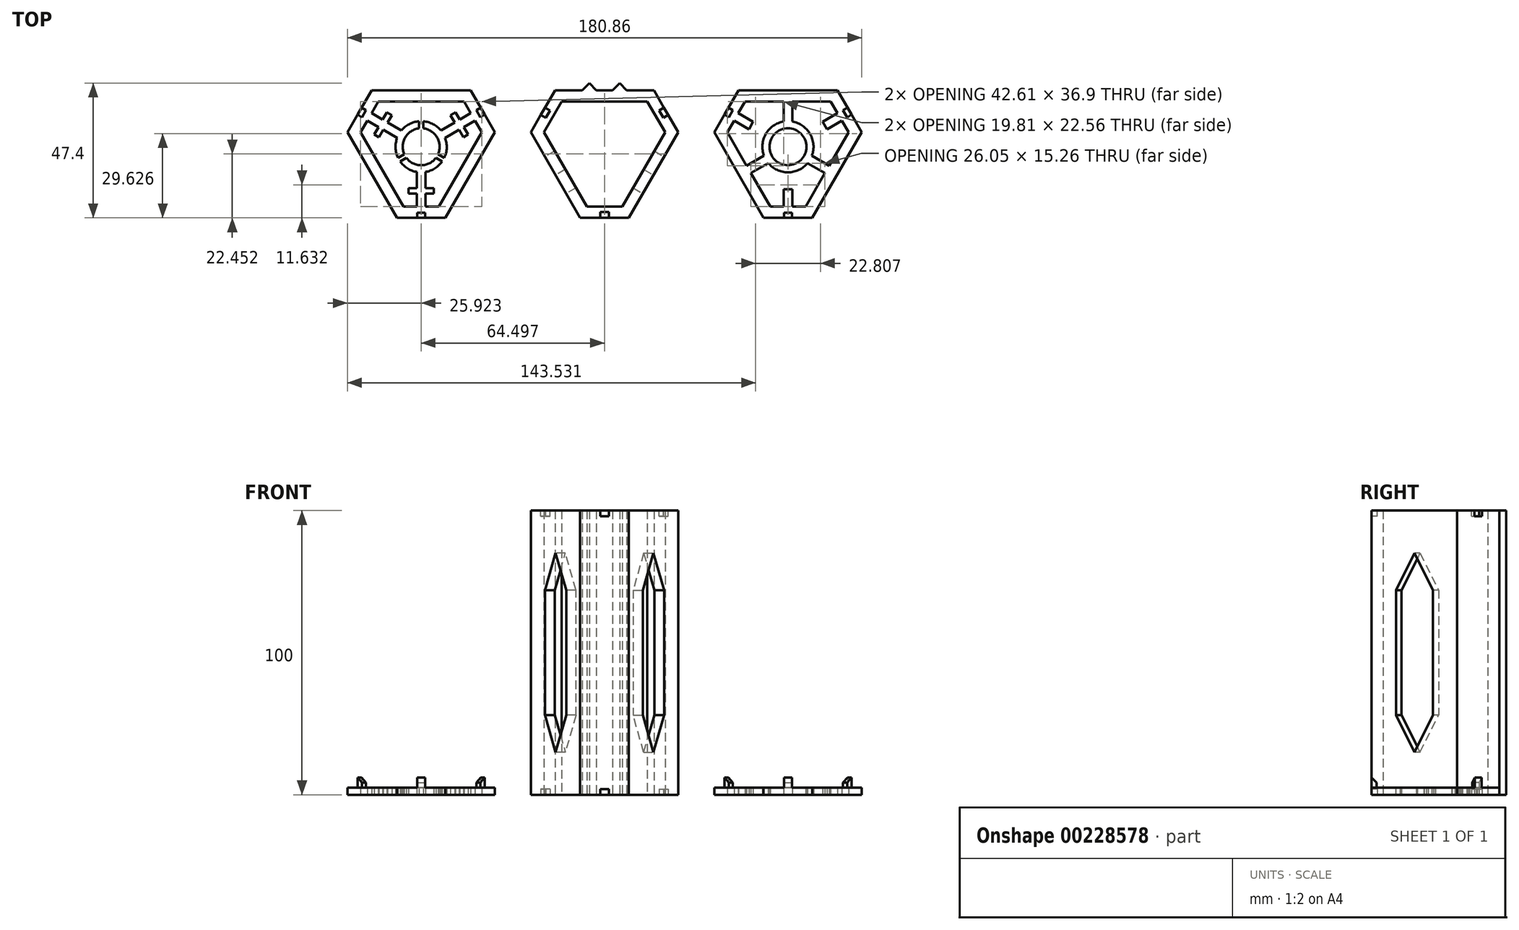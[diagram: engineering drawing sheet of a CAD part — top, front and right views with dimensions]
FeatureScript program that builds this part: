
annotation { "Feature Type Name" : "Feature", "Feature Type Description" : "" }
export const myFeature = defineFeature(function(context is Context, id is Id, definition is map)
    precondition{}
    {
        {
            var Q0;
            Q0=qCreatedBy(makeId("Top.planeOp"),FACE);
            var sketch = newSketch(context, id + "F0", { "sketchPlane" : qUnion([Q0])});
            skCircle(sketch, "E0.cCircle", {"center": v(0, 0) * mm, "radius": 28.87 * mm, "construction": true});
            skLineSegment(sketch, "E0.0", {"start": v(-28.87, 0) * mm, "end": v(-14.43, 25) * mm});
            skLineSegment(sketch, "E0.1", {"start": v(-14.43, 25) * mm, "end": v(14.43, 25) * mm});
            skLineSegment(sketch, "E0.2", {"start": v(14.43, 25) * mm, "end": v(28.87, 0) * mm});
            skLineSegment(sketch, "E0.3", {"start": v(28.87, 0) * mm, "end": v(14.43, -25) * mm});
            skLineSegment(sketch, "E0.4", {"start": v(14.43, -25) * mm, "end": v(-14.43, -25) * mm});
            skLineSegment(sketch, "E0.5", {"start": v(-14.43, -25) * mm, "end": v(-28.87, 0) * mm});
            skCircle(sketch, "E1.cCircle", {"center": v(0, 0) * mm, "radius": 25 * mm, "construction": true});
            skLineSegment(sketch, "E1.0", {"start": v(-21.65, 12.5) * mm, "end": v(21.65, 12.5) * mm});
            skLineSegment(sketch, "E1.1", {"start": v(21.65, 12.5) * mm, "end": v(0, -25) * mm});
            skLineSegment(sketch, "E1.2", {"start": v(0, -25) * mm, "end": v(-21.65, 12.5) * mm});
            skLineSegment(sketch, "E2", {"start": v(-23.62, 9.1) * mm, "end": v(-3.93, -25) * mm});
            skLineSegment(sketch, "E3", {"start": v(-19.69, 15.9) * mm, "end": v(19.69, 15.9) * mm});
            skLineSegment(sketch, "E4", {"start": v(23.62, 9.1) * mm, "end": v(3.93, -25) * mm});
            skLineSegment(sketch, "E5", {"start": v(-25.93, 5.1) * mm, "end": v(-8.55, -25) * mm});
            skLineSegment(sketch, "E6", {"start": v(8.55, -25) * mm, "end": v(25.93, 5.1) * mm});
            skLineSegment(sketch, "E7", {"start": v(-17.38, 19.9) * mm, "end": v(17.38, 19.9) * mm});
            skLineSegment(sketch, "E8", {"start": v(-6.24, -21) * mm, "end": v(6.24, -21) * mm});
            skLineSegment(sketch, "E9", {"start": v(21.3, 5.1) * mm, "end": v(15.07, 15.9) * mm});
            skLineSegment(sketch, "E10", {"start": v(-15.07, 15.9) * mm, "end": v(-21.3, 5.1) * mm});
            skCircle(sketch, "E11.cCircle", {"center": v(-64.5, 0) * mm, "radius": 28.87 * mm, "construction": true});
            skLineSegment(sketch, "E11.0", {"start": v(-93.36, 0) * mm, "end": v(-78.93, 25) * mm});
            skLineSegment(sketch, "E11.1", {"start": v(-78.93, 25) * mm, "end": v(-50.06, 25) * mm});
            skLineSegment(sketch, "E11.2", {"start": v(-50.06, 25) * mm, "end": v(-35.63, 0) * mm});
            skLineSegment(sketch, "E11.3", {"start": v(-35.63, 0) * mm, "end": v(-50.06, -25) * mm});
            skLineSegment(sketch, "E11.4", {"start": v(-50.06, -25) * mm, "end": v(-78.93, -25) * mm});
            skLineSegment(sketch, "E11.5", {"start": v(-78.93, -25) * mm, "end": v(-93.36, 0) * mm});
            skCircle(sketch, "E12.cCircle", {"center": v(-64.5, 0) * mm, "radius": 25 * mm, "construction": true});
            skLineSegment(sketch, "E12.0", {"start": v(-86.15, 12.5) * mm, "end": v(-42.85, 12.5) * mm});
            skLineSegment(sketch, "E12.1", {"start": v(-42.85, 12.5) * mm, "end": v(-64.5, -25) * mm});
            skLineSegment(sketch, "E12.2", {"start": v(-64.5, -25) * mm, "end": v(-86.15, 12.5) * mm});
            skLineSegment(sketch, "E13", {"start": v(-88.11, 9.1) * mm, "end": v(-68.43, -25) * mm});
            skLineSegment(sketch, "E14", {"start": v(-84.18, 15.9) * mm, "end": v(-44.81, 15.9) * mm});
            skLineSegment(sketch, "E15", {"start": v(-40.88, 9.1) * mm, "end": v(-60.57, -25) * mm});
            skLineSegment(sketch, "E16", {"start": v(-90.42, 5.1) * mm, "end": v(-73.05, -25) * mm});
            skLineSegment(sketch, "E17", {"start": v(-55.95, -25) * mm, "end": v(-38.57, 5.1) * mm});
            skLineSegment(sketch, "E18", {"start": v(-81.87, 19.9) * mm, "end": v(-47.12, 19.9) * mm});
            skLineSegment(sketch, "E19", {"start": v(-70.74, -21) * mm, "end": v(-58.26, -21) * mm});
            skLineSegment(sketch, "E20", {"start": v(-43.2, 5.1) * mm, "end": v(-49.43, 15.9) * mm});
            skLineSegment(sketch, "E21", {"start": v(-79.56, 15.9) * mm, "end": v(-85.8, 5.1) * mm});
            skCircle(sketch, "E22.cCircle", {"center": v(64.51, 0) * mm, "radius": 28.87 * mm, "construction": true});
            skLineSegment(sketch, "E22.0", {"start": v(35.65, 0) * mm, "end": v(50.08, 25) * mm});
            skLineSegment(sketch, "E22.1", {"start": v(50.08, 25) * mm, "end": v(78.95, 25) * mm});
            skLineSegment(sketch, "E22.2", {"start": v(78.95, 25) * mm, "end": v(93.38, 0) * mm});
            skLineSegment(sketch, "E22.3", {"start": v(93.38, 0) * mm, "end": v(78.95, -25) * mm});
            skLineSegment(sketch, "E22.4", {"start": v(78.95, -25) * mm, "end": v(50.08, -25) * mm});
            skLineSegment(sketch, "E22.5", {"start": v(50.08, -25) * mm, "end": v(35.65, 0) * mm});
            skCircle(sketch, "E23.cCircle", {"center": v(64.51, 0) * mm, "radius": 25 * mm, "construction": true});
            skLineSegment(sketch, "E23.0", {"start": v(42.86, 12.5) * mm, "end": v(86.17, 12.5) * mm});
            skLineSegment(sketch, "E23.1", {"start": v(86.17, 12.5) * mm, "end": v(64.51, -25) * mm});
            skLineSegment(sketch, "E23.2", {"start": v(64.51, -25) * mm, "end": v(42.86, 12.5) * mm});
            skLineSegment(sketch, "E24", {"start": v(40.9, 9.1) * mm, "end": v(60.58, -25) * mm});
            skLineSegment(sketch, "E25", {"start": v(44.83, 15.9) * mm, "end": v(84.2, 15.9) * mm});
            skLineSegment(sketch, "E26", {"start": v(88.13, 9.1) * mm, "end": v(68.45, -25) * mm});
            skLineSegment(sketch, "E27", {"start": v(38.59, 5.1) * mm, "end": v(55.97, -25) * mm});
            skLineSegment(sketch, "E28", {"start": v(73.06, -25) * mm, "end": v(90.44, 5.1) * mm});
            skLineSegment(sketch, "E29", {"start": v(47.14, 19.9) * mm, "end": v(81.9, 19.9) * mm});
            skLineSegment(sketch, "E30", {"start": v(58.27, -21) * mm, "end": v(70.75, -21) * mm});
            skLineSegment(sketch, "E31", {"start": v(85.82, 5.1) * mm, "end": v(79.58, 15.9) * mm});
            skLineSegment(sketch, "E32", {"start": v(49.45, 15.9) * mm, "end": v(43.2, 5.1) * mm});
            skCircle(sketch, "E33", {"center": v(-64.5, 0) * mm, "radius": 9 * mm});
            skCircle(sketch, "E34", {"center": v(64.51, 0) * mm, "radius": 9 * mm});
            skCircle(sketch, "E35", {"center": v(64.51, 0) * mm, "radius": 6.5 * mm});
            skCircle(sketch, "E36", {"center": v(-64.5, 0) * mm, "radius": 6.5 * mm});
            skPoint(sketch, "E37.startSnap0", {"position": v(53.69, -6.25) * mm});
            skLineSegment(sketch, "E38", {"start": v(51.5, -9.25) * mm, "end": v(57.58, -5.74) * mm});
            skLineSegment(sketch, "E39", {"start": v(50, -6.65) * mm, "end": v(56.08, -3.14) * mm});
            skLineSegment(sketch, "E40", {"start": v(63.01, 15.9) * mm, "end": v(63.01, 8.87) * mm});
            skLineSegment(sketch, "E41", {"start": v(66.01, 15.9) * mm, "end": v(66.01, 8.87) * mm});
            skLineSegment(sketch, "E42", {"start": v(71.45, -5.74) * mm, "end": v(77.54, -9.25) * mm});
            skLineSegment(sketch, "E43", {"start": v(79.04, -6.65) * mm, "end": v(72.95, -3.14) * mm});
            skLineSegment(sketch, "E44", {"start": v(-66, -21) * mm, "end": v(-66, -8.87) * mm});
            skLineSegment(sketch, "E45", {"start": v(-63, -21) * mm, "end": v(-63, -8.87) * mm});
            skLineSegment(sketch, "E46", {"start": v(-47.06, 11.8) * mm, "end": v(-57.56, 5.74) * mm});
            skLineSegment(sketch, "E47", {"start": v(-45.56, 9.2) * mm, "end": v(-56.06, 3.14) * mm});
            skLineSegment(sketch, "E48", {"start": v(-83.43, 9.2) * mm, "end": v(-72.93, 3.14) * mm});
            skLineSegment(sketch, "E49", {"start": v(-81.93, 11.8) * mm, "end": v(-71.43, 5.74) * mm});
            skLineSegment(sketch, "E50", {"start": v(-74.95, -6.9) * mm, "end": v(-69.71, -3.88) * mm});
            skLineSegment(sketch, "E51", {"start": v(-75.7, -5.6) * mm, "end": v(-70.46, -2.58) * mm});
            skLineSegment(sketch, "E52", {"start": v(-54.05, -6.9) * mm, "end": v(-59.28, -3.88) * mm});
            skLineSegment(sketch, "E53", {"start": v(-53.3, -5.6) * mm, "end": v(-58.53, -2.58) * mm});
            skLineSegment(sketch, "E54", {"start": v(-65.25, 12.5) * mm, "end": v(-65.25, 6.46) * mm});
            skLineSegment(sketch, "E55", {"start": v(-63.75, 12.5) * mm, "end": v(-63.75, 6.46) * mm});
            skLineSegment(sketch, "E56", {"start": v(86.17, 12.5) * mm, "end": v(72.3, 4.5) * mm});
            skLineSegment(sketch, "E57", {"start": v(42.86, 12.5) * mm, "end": v(56.72, 4.5) * mm});
            skLineSegment(sketch, "E58", {"start": v(64.51, -25) * mm, "end": v(64.51, -9) * mm});
            skLineSegment(sketch, "E59", {"start": v(51.52, 7.5) * mm, "end": v(52.27, 8.8) * mm});
            skLineSegment(sketch, "E60", {"start": v(51.52, 7.5) * mm, "end": v(50.77, 6.2) * mm});
            skLineSegment(sketch, "E61", {"start": v(77.5, 7.5) * mm, "end": v(76.76, 8.8) * mm});
            skLineSegment(sketch, "E62", {"start": v(77.5, 7.5) * mm, "end": v(78.26, 6.2) * mm});
            skLineSegment(sketch, "E63", {"start": v(64.51, -15) * mm, "end": v(63.01, -15) * mm});
            skLineSegment(sketch, "E64", {"start": v(64.51, -15) * mm, "end": v(66.01, -15) * mm});
            skLineSegment(sketch, "E65", {"start": v(50.77, 6.2) * mm, "end": v(45.58, 9.2) * mm});
            skLineSegment(sketch, "E66", {"start": v(52.27, 8.8) * mm, "end": v(47.08, 11.8) * mm});
            skLineSegment(sketch, "E67", {"start": v(76.76, 8.8) * mm, "end": v(81.95, 11.8) * mm});
            skLineSegment(sketch, "E68", {"start": v(78.26, 6.2) * mm, "end": v(83.45, 9.2) * mm});
            skLineSegment(sketch, "E69", {"start": v(66.01, -15) * mm, "end": v(66.01, -21) * mm});
            skLineSegment(sketch, "E70", {"start": v(63.01, -15) * mm, "end": v(63.01, -21) * mm});
            skLineSegment(sketch, "E71", {"start": v(-78.04, 9.55) * mm, "end": v(-76.54, 12.15) * mm});
            skLineSegment(sketch, "E72", {"start": v(-79.54, 6.95) * mm, "end": v(-81.04, 4.35) * mm});
            skLineSegment(sketch, "E73", {"start": v(-66, -16.5) * mm, "end": v(-69, -16.5) * mm});
            skLineSegment(sketch, "E74", {"start": v(-63, -16.5) * mm, "end": v(-60, -16.5) * mm});
            skLineSegment(sketch, "E75", {"start": v(-51.19, 5.95) * mm, "end": v(-49.69, 3.35) * mm});
            skLineSegment(sketch, "E76", {"start": v(-52.69, 8.55) * mm, "end": v(-54.19, 11.15) * mm});
            skLineSegment(sketch, "E77", {"start": v(-81.04, 4.35) * mm, "end": v(-79.3, 3.35) * mm});
            skLineSegment(sketch, "E78", {"start": v(-79.3, 3.35) * mm, "end": v(-77.8, 5.95) * mm});
            skLineSegment(sketch, "E79", {"start": v(-76.54, 12.15) * mm, "end": v(-74.8, 11.15) * mm});
            skLineSegment(sketch, "E80", {"start": v(-74.8, 11.15) * mm, "end": v(-76.3, 8.55) * mm});
            skLineSegment(sketch, "E81", {"start": v(-54.19, 11.15) * mm, "end": v(-52.46, 12.15) * mm});
            skLineSegment(sketch, "E82", {"start": v(-52.46, 12.15) * mm, "end": v(-50.96, 9.55) * mm});
            skLineSegment(sketch, "E83", {"start": v(-49.69, 3.35) * mm, "end": v(-47.96, 4.35) * mm});
            skLineSegment(sketch, "E84", {"start": v(-47.96, 4.35) * mm, "end": v(-49.46, 6.95) * mm});
            skLineSegment(sketch, "E85", {"start": v(-69, -16.5) * mm, "end": v(-69, -14.5) * mm});
            skLineSegment(sketch, "E86", {"start": v(-69, -14.5) * mm, "end": v(-66, -14.5) * mm});
            skLineSegment(sketch, "E87", {"start": v(-60, -16.5) * mm, "end": v(-60, -14.5) * mm});
            skLineSegment(sketch, "E88", {"start": v(-60, -14.5) * mm, "end": v(-63, -14.5) * mm});
            skLineSegment(sketch, "E89", {"start": v(-78.04, 9.55) * mm, "end": v(-79.54, 6.95) * mm});
            skLineSegment(sketch, "E90", {"start": v(-50.96, 9.55) * mm, "end": v(-49.46, 6.95) * mm});
            skLineSegment(sketch, "E91", {"start": v(-63, -16.5) * mm, "end": v(-66, -16.5) * mm});
            skLineSegment(sketch, "E92", {"start": v(-78.79, 8.25) * mm, "end": v(-82.68, 10.5) * mm});
            skLineSegment(sketch, "E93", {"start": v(-46.31, 10.5) * mm, "end": v(-50.2, 8.25) * mm});
            skLineSegment(sketch, "E94", {"start": v(-64.5, -16.5) * mm, "end": v(-64.5, -21) * mm});
            skLineSegment(sketch, "E95", {"start": v(0, 19.9) * mm, "end": v(-2.84, 19.9) * mm});
            skLineSegment(sketch, "E96", {"start": v(0, 19.9) * mm, "end": v(2.84, 19.9) * mm});
            skLineSegment(sketch, "E97", {"start": v(2.84, 19.9) * mm, "end": v(5.34, 22.4) * mm});
            skLineSegment(sketch, "E98", {"start": v(5.34, 22.4) * mm, "end": v(7.84, 19.9) * mm});
            skLineSegment(sketch, "E99", {"start": v(-2.84, 19.9) * mm, "end": v(-5.34, 22.4) * mm});
            skLineSegment(sketch, "E100", {"start": v(-5.34, 22.4) * mm, "end": v(-7.84, 19.9) * mm});
            skLineSegment(sketch, "E101", {"start": v(-86.15, 12.5) * mm, "end": v(-84.59, 11.6) * mm});
            skLineSegment(sketch, "E102", {"start": v(-84.59, 11.6) * mm, "end": v(-83.89, 12.81) * mm});
            skLineSegment(sketch, "E103", {"start": v(-83.89, 12.81) * mm, "end": v(-85.45, 13.71) * mm});
            skLineSegment(sketch, "E104", {"start": v(-42.85, 12.5) * mm, "end": v(-44.4, 11.6) * mm});
            skLineSegment(sketch, "E105", {"start": v(-44.4, 11.6) * mm, "end": v(-45.1, 12.81) * mm});
            skLineSegment(sketch, "E106", {"start": v(-44.4, 11.6) * mm, "end": v(-43.7, 10.39) * mm});
            skLineSegment(sketch, "E107", {"start": v(-43.7, 10.39) * mm, "end": v(-42.15, 11.29) * mm});
            skLineSegment(sketch, "E108", {"start": v(-64.5, -25) * mm, "end": v(-64.5, -23.2) * mm});
            skLineSegment(sketch, "E109", {"start": v(-64.5, -23.2) * mm, "end": v(-65.9, -23.2) * mm});
            skLineSegment(sketch, "E110", {"start": v(-65.9, -23.2) * mm, "end": v(-65.9, -25) * mm});
            skLineSegment(sketch, "E111", {"start": v(-64.5, -23.2) * mm, "end": v(-63.1, -23.2) * mm});
            skLineSegment(sketch, "E112", {"start": v(-63.1, -23.2) * mm, "end": v(-63.1, -25) * mm});
            skLineSegment(sketch, "E113", {"start": v(-84.59, 11.6) * mm, "end": v(-85.29, 10.39) * mm});
            skLineSegment(sketch, "E114", {"start": v(-85.29, 10.39) * mm, "end": v(-86.85, 11.29) * mm});
            skLineSegment(sketch, "E115", {"start": v(-45.1, 12.81) * mm, "end": v(-43.55, 13.71) * mm});
            skLineSegment(sketch, "E116", {"start": v(84.6, 11.6) * mm, "end": v(83.9, 12.81) * mm});
            skLineSegment(sketch, "E117", {"start": v(83.9, 12.81) * mm, "end": v(85.47, 13.71) * mm});
            skLineSegment(sketch, "E118", {"start": v(84.6, 11.6) * mm, "end": v(85.3, 10.39) * mm});
            skLineSegment(sketch, "E119", {"start": v(85.3, 10.39) * mm, "end": v(86.87, 11.29) * mm});
            skLineSegment(sketch, "E120", {"start": v(64.51, -23.2) * mm, "end": v(65.91, -23.2) * mm});
            skLineSegment(sketch, "E121", {"start": v(65.91, -23.2) * mm, "end": v(65.91, -25) * mm});
            skLineSegment(sketch, "E122", {"start": v(64.51, -23.2) * mm, "end": v(63.11, -23.2) * mm});
            skLineSegment(sketch, "E123", {"start": v(63.11, -23.2) * mm, "end": v(63.11, -25) * mm});
            skLineSegment(sketch, "E124", {"start": v(44.42, 11.6) * mm, "end": v(45.12, 12.81) * mm});
            skLineSegment(sketch, "E125", {"start": v(45.12, 12.81) * mm, "end": v(43.56, 13.71) * mm});
            skLineSegment(sketch, "E126", {"start": v(44.42, 11.6) * mm, "end": v(43.72, 10.39) * mm});
            skLineSegment(sketch, "E127", {"start": v(43.72, 10.39) * mm, "end": v(42.16, 11.29) * mm});
            skSolve(sketch);
        }
        {
            var Q0;
            {var subQ1=sQuery(id+"F0.wireOp",EDGE,"E0.0");var subQ3=sQuery(id+"F0.wireOp",EDGE,"E2");var subQ4=makeQuery(id+"F0.imprint","INTERSECT",VERTEX,{"derivedFrom":[subQ1,subQ3]});Q0=makeQuery(id+"F0.imprint","IMPRINT",FACE,{"disambiguationData":[TD([[makeQuery(id+"F0.imprint","IMPRINT",EDGE,{"disambiguationData":[TD([[subQ4,-1.0]])],"derivedFrom":subQ3}),1.0]])]});}
            var Q1;
            {var subQ1=sQuery(id+"F0.wireOp",EDGE,"E1.0");var subQ3=sQuery(id+"F0.wireOp",EDGE,"E10");var subQ4=makeQuery(id+"F0.imprint","INTERSECT",VERTEX,{"derivedFrom":[subQ1,subQ3]});Q1=makeQuery(id+"F0.imprint","IMPRINT",FACE,{"disambiguationData":[TD([[makeQuery(id+"F0.imprint","IMPRINT",EDGE,{"disambiguationData":[TD([[subQ4,-1.0]])],"derivedFrom":subQ3}),-1.0]])]});}
            var Q2;
            {var subQ1=sQuery(id+"F0.wireOp",EDGE,"E0.0");var subQ3=sQuery(id+"F0.wireOp",EDGE,"E3");var subQ4=makeQuery(id+"F0.imprint","INTERSECT",VERTEX,{"derivedFrom":[subQ1,subQ3]});Q2=makeQuery(id+"F0.imprint","IMPRINT",FACE,{"disambiguationData":[TD([[makeQuery(id+"F0.imprint","IMPRINT",EDGE,{"disambiguationData":[TD([[subQ4,-1.0]])],"derivedFrom":subQ3}),-1.0]])]});}
            var Q3;
            {var subQ6=sQuery(id+"F0.wireOp",EDGE,"E7");Q3=makeQuery(id+"F0.imprint","IMPRINT",FACE,{"disambiguationData":[TD([[makeQuery(id+"F0.imprint","IMPRINT",EDGE,{"derivedFrom":subQ6}),-1.0]])]});}
            var Q4;
            {var subQ7=sQuery(id+"F0.wireOp",EDGE,"E5");Q4=makeQuery(id+"F0.imprint","IMPRINT",FACE,{"disambiguationData":[TD([[makeQuery(id+"F0.imprint","IMPRINT",EDGE,{"derivedFrom":subQ7}),1.0]])]});}
            var Q5;
            {var subQ1=sQuery(id+"F0.wireOp",EDGE,"E0.4");var subQ3=sQuery(id+"F0.wireOp",EDGE,"E2");var subQ4=makeQuery(id+"F0.imprint","INTERSECT",VERTEX,{"derivedFrom":[subQ1,subQ3]});Q5=makeQuery(id+"F0.imprint","IMPRINT",FACE,{"disambiguationData":[TD([[makeQuery(id+"F0.imprint","IMPRINT",EDGE,{"disambiguationData":[TD([[subQ4,1.0]])],"derivedFrom":subQ3}),1.0]])]});}
            var Q6;
            {var subQ1=sQuery(id+"F0.wireOp",EDGE,"E1.1");var subQ3=sQuery(id+"F0.wireOp",EDGE,"E8");var subQ4=makeQuery(id+"F0.imprint","INTERSECT",VERTEX,{"derivedFrom":[subQ1,subQ3]});Q6=makeQuery(id+"F0.imprint","IMPRINT",FACE,{"disambiguationData":[TD([[makeQuery(id+"F0.imprint","IMPRINT",EDGE,{"disambiguationData":[TD([[subQ4,1.0]])],"derivedFrom":subQ3}),-1.0]])]});}
            var Q7;
            {var subQ1=sQuery(id+"F0.wireOp",EDGE,"E0.4");var subQ3=sQuery(id+"F0.wireOp",EDGE,"E4");var subQ4=makeQuery(id+"F0.imprint","INTERSECT",VERTEX,{"derivedFrom":[subQ1,subQ3]});Q7=makeQuery(id+"F0.imprint","IMPRINT",FACE,{"disambiguationData":[TD([[makeQuery(id+"F0.imprint","IMPRINT",EDGE,{"disambiguationData":[TD([[subQ4,1.0]])],"derivedFrom":subQ3}),-1.0]])]});}
            var Q8;
            {var subQ1=sQuery(id+"F0.wireOp",EDGE,"E0.2");var subQ3=sQuery(id+"F0.wireOp",EDGE,"E4");var subQ4=makeQuery(id+"F0.imprint","INTERSECT",VERTEX,{"derivedFrom":[subQ1,subQ3]});Q8=makeQuery(id+"F0.imprint","IMPRINT",FACE,{"disambiguationData":[TD([[makeQuery(id+"F0.imprint","IMPRINT",EDGE,{"disambiguationData":[TD([[subQ4,-1.0]])],"derivedFrom":subQ3}),-1.0]])]});}
            var Q9;
            {var subQ1=sQuery(id+"F0.wireOp",EDGE,"E1.0");var subQ3=sQuery(id+"F0.wireOp",EDGE,"E9");var subQ4=makeQuery(id+"F0.imprint","INTERSECT",VERTEX,{"derivedFrom":[subQ1,subQ3]});Q9=makeQuery(id+"F0.imprint","IMPRINT",FACE,{"disambiguationData":[TD([[makeQuery(id+"F0.imprint","IMPRINT",EDGE,{"disambiguationData":[TD([[subQ4,1.0]])],"derivedFrom":subQ3}),-1.0]])]});}
            var Q10;
            {var subQ1=sQuery(id+"F0.wireOp",EDGE,"E0.2");var subQ3=sQuery(id+"F0.wireOp",EDGE,"E3");var subQ4=makeQuery(id+"F0.imprint","INTERSECT",VERTEX,{"derivedFrom":[subQ1,subQ3]});Q10=makeQuery(id+"F0.imprint","IMPRINT",FACE,{"disambiguationData":[TD([[makeQuery(id+"F0.imprint","IMPRINT",EDGE,{"disambiguationData":[TD([[subQ4,1.0]])],"derivedFrom":subQ3}),-1.0]])]});}
            var Q11;
            {var subQ7=sQuery(id+"F0.wireOp",EDGE,"E6");Q11=makeQuery(id+"F0.imprint","IMPRINT",FACE,{"disambiguationData":[TD([[makeQuery(id+"F0.imprint","IMPRINT",EDGE,{"derivedFrom":subQ7}),1.0]])]});}
            var Q12;
            {var subQ0=sQuery(id+"F0.wireOp",EDGE,"E99");Q12=makeQuery(id+"F0.imprint","IMPRINT",FACE,{"disambiguationData":[TD([[makeQuery(id+"F0.imprint","IMPRINT",EDGE,{"derivedFrom":subQ0}),1.0]])]});}
            var Q13;
            {var subQ0=sQuery(id+"F0.wireOp",EDGE,"E97");Q13=makeQuery(id+"F0.imprint","IMPRINT",FACE,{"disambiguationData":[TD([[makeQuery(id+"F0.imprint","IMPRINT",EDGE,{"derivedFrom":subQ0}),-1.0]])]});}
            extrude(context, id + "F1", {"entities" : qUnion([Q0, Q1, Q2, Q3, Q4, Q5, Q6, Q7, Q8, Q9, Q10, Q11, Q12, Q13]), "depth" : 100 * mm});
        }
        {
            var Q0;
            {var subQ3=sQuery(id+"F0.wireOp",EDGE,"E27");Q0=makeQuery(id+"F0.imprint","IMPRINT",FACE,{"disambiguationData":[TD([[makeQuery(id+"F0.imprint","IMPRINT",EDGE,{"derivedFrom":subQ3}),1.0]])]});}
            var Q1;
            {var subQ1=sQuery(id+"F0.wireOp",EDGE,"E22.0");var subQ3=sQuery(id+"F0.wireOp",EDGE,"E24");var subQ4=makeQuery(id+"F0.imprint","INTERSECT",VERTEX,{"derivedFrom":[subQ1,subQ3]});Q1=makeQuery(id+"F0.imprint","IMPRINT",FACE,{"disambiguationData":[TD([[makeQuery(id+"F0.imprint","IMPRINT",EDGE,{"disambiguationData":[TD([[subQ4,-1.0]])],"derivedFrom":subQ3}),1.0]])]});}
            var Q2;
            {var subQ1=sQuery(id+"F0.wireOp",EDGE,"E23.0");var subQ3=sQuery(id+"F0.wireOp",EDGE,"E32");var subQ4=makeQuery(id+"F0.imprint","INTERSECT",VERTEX,{"derivedFrom":[subQ1,subQ3]});Q2=makeQuery(id+"F0.imprint","IMPRINT",FACE,{"disambiguationData":[TD([[makeQuery(id+"F0.imprint","IMPRINT",EDGE,{"disambiguationData":[TD([[subQ4,-1.0]])],"derivedFrom":subQ3}),-1.0]])]});}
            var Q3;
            {var subQ1=sQuery(id+"F0.wireOp",EDGE,"E22.0");var subQ3=sQuery(id+"F0.wireOp",EDGE,"E25");var subQ4=makeQuery(id+"F0.imprint","INTERSECT",VERTEX,{"derivedFrom":[subQ1,subQ3]});Q3=makeQuery(id+"F0.imprint","IMPRINT",FACE,{"disambiguationData":[TD([[makeQuery(id+"F0.imprint","IMPRINT",EDGE,{"disambiguationData":[TD([[subQ4,-1.0]])],"derivedFrom":subQ3}),-1.0]])]});}
            var Q4;
            {var subQ1=sQuery(id+"F0.wireOp",EDGE,"E22.2");var subQ3=sQuery(id+"F0.wireOp",EDGE,"E25");var subQ4=makeQuery(id+"F0.imprint","INTERSECT",VERTEX,{"derivedFrom":[subQ1,subQ3]});Q4=makeQuery(id+"F0.imprint","IMPRINT",FACE,{"disambiguationData":[TD([[makeQuery(id+"F0.imprint","IMPRINT",EDGE,{"disambiguationData":[TD([[subQ4,1.0]])],"derivedFrom":subQ3}),-1.0]])]});}
            var Q5;
            {var subQ1=sQuery(id+"F0.wireOp",EDGE,"E23.0");var subQ3=sQuery(id+"F0.wireOp",EDGE,"E31");var subQ4=makeQuery(id+"F0.imprint","INTERSECT",VERTEX,{"derivedFrom":[subQ1,subQ3]});Q5=makeQuery(id+"F0.imprint","IMPRINT",FACE,{"disambiguationData":[TD([[makeQuery(id+"F0.imprint","IMPRINT",EDGE,{"disambiguationData":[TD([[subQ4,1.0]])],"derivedFrom":subQ3}),-1.0]])]});}
            var Q6;
            {var subQ1=sQuery(id+"F0.wireOp",EDGE,"E22.2");var subQ3=sQuery(id+"F0.wireOp",EDGE,"E26");var subQ4=makeQuery(id+"F0.imprint","INTERSECT",VERTEX,{"derivedFrom":[subQ1,subQ3]});Q6=makeQuery(id+"F0.imprint","IMPRINT",FACE,{"disambiguationData":[TD([[makeQuery(id+"F0.imprint","IMPRINT",EDGE,{"disambiguationData":[TD([[subQ4,-1.0]])],"derivedFrom":subQ3}),-1.0]])]});}
            var Q7;
            {var subQ1=sQuery(id+"F0.wireOp",EDGE,"E22.4");var subQ3=sQuery(id+"F0.wireOp",EDGE,"E26");var subQ4=makeQuery(id+"F0.imprint","INTERSECT",VERTEX,{"derivedFrom":[subQ1,subQ3]});Q7=makeQuery(id+"F0.imprint","IMPRINT",FACE,{"disambiguationData":[TD([[makeQuery(id+"F0.imprint","IMPRINT",EDGE,{"disambiguationData":[TD([[subQ4,1.0]])],"derivedFrom":subQ3}),-1.0]])]});}
            var Q8;
            {var subQ7=sQuery(id+"F0.wireOp",EDGE,"E28");Q8=makeQuery(id+"F0.imprint","IMPRINT",FACE,{"disambiguationData":[TD([[makeQuery(id+"F0.imprint","IMPRINT",EDGE,{"derivedFrom":subQ7}),1.0]])]});}
            var Q9;
            {var subQ1=sQuery(id+"F0.wireOp",EDGE,"E23.1");var subQ3=sQuery(id+"F0.wireOp",EDGE,"E30");var subQ4=makeQuery(id+"F0.imprint","INTERSECT",VERTEX,{"derivedFrom":[subQ1,subQ3]});Q9=makeQuery(id+"F0.imprint","IMPRINT",FACE,{"disambiguationData":[TD([[makeQuery(id+"F0.imprint","IMPRINT",EDGE,{"disambiguationData":[TD([[subQ4,1.0]])],"derivedFrom":subQ3}),-1.0]])]});}
            var Q10;
            {var subQ1=sQuery(id+"F0.wireOp",EDGE,"E22.4");var subQ3=sQuery(id+"F0.wireOp",EDGE,"E24");var subQ4=makeQuery(id+"F0.imprint","INTERSECT",VERTEX,{"derivedFrom":[subQ1,subQ3]});Q10=makeQuery(id+"F0.imprint","IMPRINT",FACE,{"disambiguationData":[TD([[makeQuery(id+"F0.imprint","IMPRINT",EDGE,{"disambiguationData":[TD([[subQ4,1.0]])],"derivedFrom":subQ3}),1.0]])]});}
            var Q11;
            Q11=makeQuery(id+"F0.imprint","IMPRINT",FACE,{"disambiguationData":[TD([[makeQuery(id+"F0.imprint","IMPRINT",EDGE,{"derivedFrom":sQuery(id+"F0.wireOp",EDGE,"E34")}),1.0]])]});
            var Q12;
            {var subQ3=sQuery(id+"F0.wireOp",EDGE,"E18");Q12=makeQuery(id+"F0.imprint","IMPRINT",FACE,{"disambiguationData":[TD([[makeQuery(id+"F0.imprint","IMPRINT",EDGE,{"derivedFrom":subQ3}),-1.0]])]});}
            var Q13;
            {var subQ1=sQuery(id+"F0.wireOp",EDGE,"E11.0");var subQ3=sQuery(id+"F0.wireOp",EDGE,"E14");var subQ4=makeQuery(id+"F0.imprint","INTERSECT",VERTEX,{"derivedFrom":[subQ1,subQ3]});Q13=makeQuery(id+"F0.imprint","IMPRINT",FACE,{"disambiguationData":[TD([[makeQuery(id+"F0.imprint","IMPRINT",EDGE,{"disambiguationData":[TD([[subQ4,-1.0]])],"derivedFrom":subQ3}),-1.0]])]});}
            var Q14;
            {var subQ1=sQuery(id+"F0.wireOp",EDGE,"E12.0");var subQ3=sQuery(id+"F0.wireOp",EDGE,"E21");var subQ4=makeQuery(id+"F0.imprint","INTERSECT",VERTEX,{"derivedFrom":[subQ1,subQ3]});Q14=makeQuery(id+"F0.imprint","IMPRINT",FACE,{"disambiguationData":[TD([[makeQuery(id+"F0.imprint","IMPRINT",EDGE,{"disambiguationData":[TD([[subQ4,-1.0]])],"derivedFrom":subQ3}),-1.0]])]});}
            var Q15;
            {var subQ1=sQuery(id+"F0.wireOp",EDGE,"E11.0");var subQ3=sQuery(id+"F0.wireOp",EDGE,"E13");var subQ4=makeQuery(id+"F0.imprint","INTERSECT",VERTEX,{"derivedFrom":[subQ1,subQ3]});Q15=makeQuery(id+"F0.imprint","IMPRINT",FACE,{"disambiguationData":[TD([[makeQuery(id+"F0.imprint","IMPRINT",EDGE,{"disambiguationData":[TD([[subQ4,-1.0]])],"derivedFrom":subQ3}),1.0]])]});}
            var Q16;
            {var subQ3=sQuery(id+"F0.wireOp",EDGE,"E16");Q16=makeQuery(id+"F0.imprint","IMPRINT",FACE,{"disambiguationData":[TD([[makeQuery(id+"F0.imprint","IMPRINT",EDGE,{"derivedFrom":subQ3}),1.0]])]});}
            var Q17;
            {var subQ1=sQuery(id+"F0.wireOp",EDGE,"E11.4");var subQ3=sQuery(id+"F0.wireOp",EDGE,"E13");var subQ4=makeQuery(id+"F0.imprint","INTERSECT",VERTEX,{"derivedFrom":[subQ1,subQ3]});Q17=makeQuery(id+"F0.imprint","IMPRINT",FACE,{"disambiguationData":[TD([[makeQuery(id+"F0.imprint","IMPRINT",EDGE,{"disambiguationData":[TD([[subQ4,1.0]])],"derivedFrom":subQ3}),1.0]])]});}
            var Q18;
            {var subQ1=sQuery(id+"F0.wireOp",EDGE,"E12.1");var subQ3=sQuery(id+"F0.wireOp",EDGE,"E19");var subQ4=makeQuery(id+"F0.imprint","INTERSECT",VERTEX,{"derivedFrom":[subQ1,subQ3]});Q18=makeQuery(id+"F0.imprint","IMPRINT",FACE,{"disambiguationData":[TD([[makeQuery(id+"F0.imprint","IMPRINT",EDGE,{"disambiguationData":[TD([[subQ4,1.0]])],"derivedFrom":subQ3}),-1.0]])]});}
            var Q19;
            {var subQ1=sQuery(id+"F0.wireOp",EDGE,"E11.4");var subQ3=sQuery(id+"F0.wireOp",EDGE,"E15");var subQ4=makeQuery(id+"F0.imprint","INTERSECT",VERTEX,{"derivedFrom":[subQ1,subQ3]});Q19=makeQuery(id+"F0.imprint","IMPRINT",FACE,{"disambiguationData":[TD([[makeQuery(id+"F0.imprint","IMPRINT",EDGE,{"disambiguationData":[TD([[subQ4,1.0]])],"derivedFrom":subQ3}),-1.0]])]});}
            var Q20;
            {var subQ7=sQuery(id+"F0.wireOp",EDGE,"E17");Q20=makeQuery(id+"F0.imprint","IMPRINT",FACE,{"disambiguationData":[TD([[makeQuery(id+"F0.imprint","IMPRINT",EDGE,{"derivedFrom":subQ7}),1.0]])]});}
            var Q21;
            {var subQ1=sQuery(id+"F0.wireOp",EDGE,"E11.2");var subQ3=sQuery(id+"F0.wireOp",EDGE,"E15");var subQ4=makeQuery(id+"F0.imprint","INTERSECT",VERTEX,{"derivedFrom":[subQ1,subQ3]});Q21=makeQuery(id+"F0.imprint","IMPRINT",FACE,{"disambiguationData":[TD([[makeQuery(id+"F0.imprint","IMPRINT",EDGE,{"disambiguationData":[TD([[subQ4,-1.0]])],"derivedFrom":subQ3}),-1.0]])]});}
            var Q22;
            {var subQ1=sQuery(id+"F0.wireOp",EDGE,"E12.0");var subQ3=sQuery(id+"F0.wireOp",EDGE,"E20");var subQ4=makeQuery(id+"F0.imprint","INTERSECT",VERTEX,{"derivedFrom":[subQ1,subQ3]});Q22=makeQuery(id+"F0.imprint","IMPRINT",FACE,{"disambiguationData":[TD([[makeQuery(id+"F0.imprint","IMPRINT",EDGE,{"disambiguationData":[TD([[subQ4,1.0]])],"derivedFrom":subQ3}),-1.0]])]});}
            var Q23;
            Q23=makeQuery(id+"F0.imprint","IMPRINT",FACE,{"disambiguationData":[TD([[makeQuery(id+"F0.imprint","IMPRINT",EDGE,{"derivedFrom":sQuery(id+"F0.wireOp",EDGE,"E33")}),1.0]])]});
            var Q24;
            {var subQ0=sQuery(id+"F0.wireOp",EDGE,"E40");var subQ1=sQuery(id+"F0.wireOp",EDGE,"E23.0");var subQ2=makeQuery(id+"F0.imprint","INTERSECT",VERTEX,{"derivedFrom":[subQ1,subQ0]});Q24=makeQuery(id+"F0.imprint","IMPRINT",FACE,{"disambiguationData":[TD([[makeQuery(id+"F0.imprint","IMPRINT",EDGE,{"disambiguationData":[TD([[subQ2,-1.0]])],"derivedFrom":subQ1}),1.0]])]});}
            var Q25;
            {var subQ5=sQuery(id+"F0.wireOp",EDGE,"E29");Q25=makeQuery(id+"F0.imprint","IMPRINT",FACE,{"disambiguationData":[TD([[makeQuery(id+"F0.imprint","IMPRINT",EDGE,{"derivedFrom":subQ5}),-1.0]])]});}
            var Q26;
            {var subQ0=sQuery(id+"F0.wireOp",EDGE,"E40");var subQ1=sQuery(id+"F0.wireOp",EDGE,"E23.0");var subQ2=makeQuery(id+"F0.imprint","INTERSECT",VERTEX,{"derivedFrom":[subQ1,subQ0]});Q26=makeQuery(id+"F0.imprint","IMPRINT",FACE,{"disambiguationData":[TD([[makeQuery(id+"F0.imprint","IMPRINT",EDGE,{"disambiguationData":[TD([[subQ2,-1.0]])],"derivedFrom":subQ1}),-1.0]])]});}
            var Q27;
            {var subQ0=sQuery(id+"F0.wireOp",EDGE,"E38");var subQ1=sQuery(id+"F0.wireOp",EDGE,"E23.2");var subQ2=makeQuery(id+"F0.imprint","INTERSECT",VERTEX,{"derivedFrom":[subQ1,subQ0]});Q27=makeQuery(id+"F0.imprint","IMPRINT",FACE,{"disambiguationData":[TD([[makeQuery(id+"F0.imprint","IMPRINT",EDGE,{"disambiguationData":[TD([[subQ2,-1.0]])],"derivedFrom":subQ1}),-1.0]])]});}
            var Q28;
            {var subQ0=sQuery(id+"F0.wireOp",EDGE,"E38");var subQ1=sQuery(id+"F0.wireOp",EDGE,"E23.2");var subQ2=makeQuery(id+"F0.imprint","INTERSECT",VERTEX,{"derivedFrom":[subQ1,subQ0]});Q28=makeQuery(id+"F0.imprint","IMPRINT",FACE,{"disambiguationData":[TD([[makeQuery(id+"F0.imprint","IMPRINT",EDGE,{"disambiguationData":[TD([[subQ2,-1.0]])],"derivedFrom":subQ1}),1.0]])]});}
            var Q29;
            {var subQ0=sQuery(id+"F0.wireOp",EDGE,"E43");var subQ1=sQuery(id+"F0.wireOp",EDGE,"E23.1");var subQ2=makeQuery(id+"F0.imprint","INTERSECT",VERTEX,{"derivedFrom":[subQ1,subQ0]});Q29=makeQuery(id+"F0.imprint","IMPRINT",FACE,{"disambiguationData":[TD([[makeQuery(id+"F0.imprint","IMPRINT",EDGE,{"disambiguationData":[TD([[subQ2,-1.0]])],"derivedFrom":subQ1}),-1.0]])]});}
            var Q30;
            {var subQ0=sQuery(id+"F0.wireOp",EDGE,"E43");var subQ1=sQuery(id+"F0.wireOp",EDGE,"E23.1");var subQ2=makeQuery(id+"F0.imprint","INTERSECT",VERTEX,{"derivedFrom":[subQ1,subQ0]});Q30=makeQuery(id+"F0.imprint","IMPRINT",FACE,{"disambiguationData":[TD([[makeQuery(id+"F0.imprint","IMPRINT",EDGE,{"disambiguationData":[TD([[subQ2,-1.0]])],"derivedFrom":subQ1}),1.0]])]});}
            var Q31;
            {var subQ0=sQuery(id+"F0.wireOp",EDGE,"E48");Q31=makeQuery(id+"F0.imprint","IMPRINT",FACE,{"disambiguationData":[TD([[makeQuery(id+"F0.imprint","IMPRINT",EDGE,{"derivedFrom":subQ0}),1.0]])]});}
            var Q32;
            {var subQ0=sQuery(id+"F0.wireOp",EDGE,"E46");Q32=makeQuery(id+"F0.imprint","IMPRINT",FACE,{"disambiguationData":[TD([[makeQuery(id+"F0.imprint","IMPRINT",EDGE,{"derivedFrom":subQ0}),1.0]])]});}
            var Q33;
            {var subQ0=sQuery(id+"F0.wireOp",EDGE,"E44");Q33=makeQuery(id+"F0.imprint","IMPRINT",FACE,{"disambiguationData":[TD([[makeQuery(id+"F0.imprint","IMPRINT",EDGE,{"derivedFrom":subQ0}),-1.0]])]});}
            var Q34;
            {var subQ3=sQuery(id+"F0.wireOp",EDGE,"E30");var subQ5=makeQuery(id+"F0.imprint","INTERSECT",VERTEX,{"derivedFrom":[subQ3,sQuery(id+"F0.wireOp",EDGE,"E70")]});Q34=makeQuery(id+"F0.imprint","IMPRINT",FACE,{"disambiguationData":[TD([[makeQuery(id+"F0.imprint","IMPRINT",EDGE,{"disambiguationData":[TD([[subQ5,1.0]])],"derivedFrom":subQ3}),-1.0]])]});}
            var Q35;
            {var subQ3=sQuery(id+"F0.wireOp",EDGE,"E32");var subQ5=makeQuery(id+"F0.imprint","INTERSECT",VERTEX,{"derivedFrom":[subQ3,sQuery(id+"F0.wireOp",EDGE,"E65")]});Q35=makeQuery(id+"F0.imprint","IMPRINT",FACE,{"disambiguationData":[TD([[makeQuery(id+"F0.imprint","IMPRINT",EDGE,{"disambiguationData":[TD([[subQ5,1.0]])],"derivedFrom":subQ3}),-1.0]])]});}
            var Q36;
            {var subQ3=sQuery(id+"F0.wireOp",EDGE,"E31");var subQ5=makeQuery(id+"F0.imprint","INTERSECT",VERTEX,{"derivedFrom":[subQ3,sQuery(id+"F0.wireOp",EDGE,"E68")]});Q36=makeQuery(id+"F0.imprint","IMPRINT",FACE,{"disambiguationData":[TD([[makeQuery(id+"F0.imprint","IMPRINT",EDGE,{"disambiguationData":[TD([[subQ5,1.0]])],"derivedFrom":subQ3}),-1.0]])]});}
            var Q37;
            {var subQ4=sQuery(id+"F0.wireOp",EDGE,"E62");Q37=makeQuery(id+"F0.imprint","IMPRINT",FACE,{"disambiguationData":[TD([[makeQuery(id+"F0.imprint","IMPRINT",EDGE,{"derivedFrom":subQ4}),1.0]])]});}
            var Q38;
            {var subQ4=sQuery(id+"F0.wireOp",EDGE,"E61");Q38=makeQuery(id+"F0.imprint","IMPRINT",FACE,{"disambiguationData":[TD([[makeQuery(id+"F0.imprint","IMPRINT",EDGE,{"derivedFrom":subQ4}),-1.0]])]});}
            var Q39;
            {var subQ4=sQuery(id+"F0.wireOp",EDGE,"E59");Q39=makeQuery(id+"F0.imprint","IMPRINT",FACE,{"disambiguationData":[TD([[makeQuery(id+"F0.imprint","IMPRINT",EDGE,{"derivedFrom":subQ4}),1.0]])]});}
            var Q40;
            {var subQ4=sQuery(id+"F0.wireOp",EDGE,"E60");Q40=makeQuery(id+"F0.imprint","IMPRINT",FACE,{"disambiguationData":[TD([[makeQuery(id+"F0.imprint","IMPRINT",EDGE,{"derivedFrom":subQ4}),-1.0]])]});}
            var Q41;
            {var subQ4=sQuery(id+"F0.wireOp",EDGE,"E63");Q41=makeQuery(id+"F0.imprint","IMPRINT",FACE,{"disambiguationData":[TD([[makeQuery(id+"F0.imprint","IMPRINT",EDGE,{"derivedFrom":subQ4}),1.0]])]});}
            var Q42;
            {var subQ4=sQuery(id+"F0.wireOp",EDGE,"E64");Q42=makeQuery(id+"F0.imprint","IMPRINT",FACE,{"disambiguationData":[TD([[makeQuery(id+"F0.imprint","IMPRINT",EDGE,{"derivedFrom":subQ4}),-1.0]])]});}
            var Q43;
            {var subQ3=sQuery(id+"F0.wireOp",EDGE,"E92");Q43=makeQuery(id+"F0.imprint","IMPRINT",FACE,{"disambiguationData":[TD([[makeQuery(id+"F0.imprint","IMPRINT",EDGE,{"derivedFrom":subQ3}),-1.0]])]});}
            var Q44;
            {var subQ3=sQuery(id+"F0.wireOp",EDGE,"E92");Q44=makeQuery(id+"F0.imprint","IMPRINT",FACE,{"disambiguationData":[TD([[makeQuery(id+"F0.imprint","IMPRINT",EDGE,{"derivedFrom":subQ3}),1.0]])]});}
            var Q45;
            {var subQ0=sQuery(id+"F0.wireOp",EDGE,"E72");Q45=makeQuery(id+"F0.imprint","IMPRINT",FACE,{"disambiguationData":[TD([[makeQuery(id+"F0.imprint","IMPRINT",EDGE,{"derivedFrom":subQ0}),1.0]])]});}
            var Q46;
            {var subQ0=sQuery(id+"F0.wireOp",EDGE,"E71");Q46=makeQuery(id+"F0.imprint","IMPRINT",FACE,{"disambiguationData":[TD([[makeQuery(id+"F0.imprint","IMPRINT",EDGE,{"derivedFrom":subQ0}),-1.0]])]});}
            var Q47;
            {var subQ0=sQuery(id+"F0.wireOp",EDGE,"E76");Q47=makeQuery(id+"F0.imprint","IMPRINT",FACE,{"disambiguationData":[TD([[makeQuery(id+"F0.imprint","IMPRINT",EDGE,{"derivedFrom":subQ0}),-1.0]])]});}
            var Q48;
            {var subQ0=sQuery(id+"F0.wireOp",EDGE,"E75");Q48=makeQuery(id+"F0.imprint","IMPRINT",FACE,{"disambiguationData":[TD([[makeQuery(id+"F0.imprint","IMPRINT",EDGE,{"derivedFrom":subQ0}),1.0]])]});}
            var Q49;
            {var subQ0=sQuery(id+"F0.wireOp",EDGE,"E74");Q49=makeQuery(id+"F0.imprint","IMPRINT",FACE,{"disambiguationData":[TD([[makeQuery(id+"F0.imprint","IMPRINT",EDGE,{"derivedFrom":subQ0}),1.0]])]});}
            var Q50;
            {var subQ0=sQuery(id+"F0.wireOp",EDGE,"E73");Q50=makeQuery(id+"F0.imprint","IMPRINT",FACE,{"disambiguationData":[TD([[makeQuery(id+"F0.imprint","IMPRINT",EDGE,{"derivedFrom":subQ0}),-1.0]])]});}
            var Q51;
            {var subQ3=sQuery(id+"F0.wireOp",EDGE,"E94");Q51=makeQuery(id+"F0.imprint","IMPRINT",FACE,{"disambiguationData":[TD([[makeQuery(id+"F0.imprint","IMPRINT",EDGE,{"derivedFrom":subQ3}),-1.0]])]});}
            var Q52;
            {var subQ3=sQuery(id+"F0.wireOp",EDGE,"E94");Q52=makeQuery(id+"F0.imprint","IMPRINT",FACE,{"disambiguationData":[TD([[makeQuery(id+"F0.imprint","IMPRINT",EDGE,{"derivedFrom":subQ3}),1.0]])]});}
            var Q53;
            {var subQ3=sQuery(id+"F0.wireOp",EDGE,"E93");Q53=makeQuery(id+"F0.imprint","IMPRINT",FACE,{"disambiguationData":[TD([[makeQuery(id+"F0.imprint","IMPRINT",EDGE,{"derivedFrom":subQ3}),-1.0]])]});}
            var Q54;
            {var subQ3=sQuery(id+"F0.wireOp",EDGE,"E93");Q54=makeQuery(id+"F0.imprint","IMPRINT",FACE,{"disambiguationData":[TD([[makeQuery(id+"F0.imprint","IMPRINT",EDGE,{"derivedFrom":subQ3}),1.0]])]});}
            var Q55;
            {var subQ5=sQuery(id+"F0.wireOp",EDGE,"E12.0");var subQ7=makeQuery(id+"F0.imprint","INTERSECT",VERTEX,{"derivedFrom":[subQ5,sQuery(id+"F0.wireOp",EDGE,"E105")]});Q55=makeQuery(id+"F0.imprint","IMPRINT",FACE,{"disambiguationData":[TD([[makeQuery(id+"F0.imprint","IMPRINT",EDGE,{"disambiguationData":[TD([[subQ7,1.0]])],"derivedFrom":subQ5}),1.0]])]});}
            extrude(context, id + "F2", {"entities" : qUnion([Q0, Q1, Q2, Q3, Q4, Q5, Q6, Q7, Q8, Q9, Q10, Q11, Q12, Q13, Q14, Q15, Q16, Q17, Q18, Q19, Q20, Q21, Q22, Q23, Q24, Q25, Q26, Q27, Q28, Q29, Q30, Q31, Q32, Q33, Q34, Q35, Q36, Q37, Q38, Q39, Q40, Q41, Q42, Q43, Q44, Q45, Q46, Q47, Q48, Q49, Q50, Q51, Q52, Q53, Q54, Q55]), "depth" : 2.5 * mm});
        }
        {
            var Q0;
            Q0=makeQuery(id+"F1.opExtrude","CAP_FACE",FACE,{"disambiguationData":[OSD([sQuery(id+"F0.wireOp",EDGE,"E0.0"),sQuery(id+"F0.wireOp",EDGE,"E0.2"),sQuery(id+"F0.wireOp",EDGE,"E0.4"),sQuery(id+"F0.wireOp",EDGE,"E2"),sQuery(id+"F0.wireOp",EDGE,"E3"),sQuery(id+"F0.wireOp",EDGE,"E4"),sQuery(id+"F0.wireOp",EDGE,"E5"),sQuery(id+"F0.wireOp",EDGE,"E6"),sQuery(id+"F0.wireOp",EDGE,"E7"),sQuery(id+"F0.wireOp",EDGE,"E8"),sQuery(id+"F0.wireOp",EDGE,"E9"),sQuery(id+"F0.wireOp",EDGE,"E10")])],"isStart":false});
            var sketch = newSketch(context, id + "F3", { "sketchPlane" : qUnion([Q0])});
            skLineSegment(sketch, "E128", {"start": v(-25.93, 5.1) * mm, "end": v(-21.65, 12.5) * mm});
            skLineSegment(sketch, "E129", {"start": v(-21.65, 12.5) * mm, "end": v(-17.38, 19.9) * mm});
            skLineSegment(sketch, "E130", {"start": v(17.38, 19.9) * mm, "end": v(21.65, 12.5) * mm});
            skLineSegment(sketch, "E131", {"start": v(21.65, 12.5) * mm, "end": v(25.93, 5.1) * mm});
            skLineSegment(sketch, "E132", {"start": v(8.55, -25) * mm, "end": v(0, -25) * mm});
            skLineSegment(sketch, "E133", {"start": v(0, -25) * mm, "end": v(-8.55, -25) * mm});
            skLineSegment(sketch, "E134", {"start": v(-21.65, 12.5) * mm, "end": v(-19.92, 11.5) * mm});
            skLineSegment(sketch, "E135", {"start": v(-19.92, 11.5) * mm, "end": v(-19.17, 12.8) * mm});
            skLineSegment(sketch, "E136", {"start": v(-19.17, 12.8) * mm, "end": v(-20.9, 13.8) * mm});
            skLineSegment(sketch, "E137", {"start": v(-19.92, 11.5) * mm, "end": v(-20.67, 10.2) * mm});
            skLineSegment(sketch, "E138", {"start": v(-20.67, 10.2) * mm, "end": v(-22.4, 11.2) * mm});
            skLineSegment(sketch, "E139", {"start": v(21.65, 12.5) * mm, "end": v(19.92, 11.5) * mm});
            skLineSegment(sketch, "E140", {"start": v(19.92, 11.5) * mm, "end": v(19.17, 12.8) * mm});
            skLineSegment(sketch, "E141", {"start": v(19.17, 12.8) * mm, "end": v(20.9, 13.8) * mm});
            skLineSegment(sketch, "E142", {"start": v(19.92, 11.5) * mm, "end": v(20.67, 10.2) * mm});
            skLineSegment(sketch, "E143", {"start": v(20.67, 10.2) * mm, "end": v(22.4, 11.2) * mm});
            skLineSegment(sketch, "E144", {"start": v(0, -25) * mm, "end": v(0, -23) * mm});
            skLineSegment(sketch, "E145", {"start": v(0, -23) * mm, "end": v(1.5, -23) * mm});
            skLineSegment(sketch, "E146", {"start": v(1.5, -23) * mm, "end": v(1.5, -25) * mm});
            skLineSegment(sketch, "E147", {"start": v(0, -23) * mm, "end": v(-1.5, -23) * mm});
            skLineSegment(sketch, "E148", {"start": v(-1.5, -23) * mm, "end": v(-1.5, -25) * mm});
            skSolve(sketch);
        }
        {
            var Q0;
            {var subQ0=sQuery(id+"F3.wireOp",EDGE,"E134");Q0=makeQuery(id+"F3.imprint","IMPRINT",FACE,{"disambiguationData":[TD([[makeQuery(id+"F3.imprint","IMPRINT",EDGE,{"derivedFrom":subQ0}),1.0]])]});}
            var Q1;
            {var subQ0=sQuery(id+"F3.wireOp",EDGE,"E134");Q1=makeQuery(id+"F3.imprint","IMPRINT",FACE,{"disambiguationData":[TD([[makeQuery(id+"F3.imprint","IMPRINT",EDGE,{"derivedFrom":subQ0}),-1.0]])]});}
            var Q2;
            {var subQ0=sQuery(id+"F3.wireOp",EDGE,"E139");Q2=makeQuery(id+"F3.imprint","IMPRINT",FACE,{"disambiguationData":[TD([[makeQuery(id+"F3.imprint","IMPRINT",EDGE,{"derivedFrom":subQ0}),-1.0]])]});}
            var Q3;
            {var subQ0=sQuery(id+"F3.wireOp",EDGE,"E139");Q3=makeQuery(id+"F3.imprint","IMPRINT",FACE,{"disambiguationData":[TD([[makeQuery(id+"F3.imprint","IMPRINT",EDGE,{"derivedFrom":subQ0}),1.0]])]});}
            var Q4;
            {var subQ0=sQuery(id+"F3.wireOp",EDGE,"E144");Q4=makeQuery(id+"F3.imprint","IMPRINT",FACE,{"disambiguationData":[TD([[makeQuery(id+"F3.imprint","IMPRINT",EDGE,{"derivedFrom":subQ0}),-1.0]])]});}
            var Q5;
            {var subQ0=sQuery(id+"F3.wireOp",EDGE,"E144");Q5=makeQuery(id+"F3.imprint","IMPRINT",FACE,{"disambiguationData":[TD([[makeQuery(id+"F3.imprint","IMPRINT",EDGE,{"derivedFrom":subQ0}),1.0]])]});}
            extrude(context, id + "F4", {"entities" : qUnion([Q0, Q1, Q2, Q3, Q4, Q5]), "oppositeDirection" : true, "depth" : 2 * mm});
        }
        {
            var Q0;
            Q0=makeQuery(id+"F1.opExtrude","CAP_FACE",FACE,{"disambiguationData":[OSD([sQuery(id+"F0.wireOp",EDGE,"E0.0"),sQuery(id+"F0.wireOp",EDGE,"E0.2"),sQuery(id+"F0.wireOp",EDGE,"E0.4"),sQuery(id+"F0.wireOp",EDGE,"E2"),sQuery(id+"F0.wireOp",EDGE,"E3"),sQuery(id+"F0.wireOp",EDGE,"E4"),sQuery(id+"F0.wireOp",EDGE,"E5"),sQuery(id+"F0.wireOp",EDGE,"E6"),sQuery(id+"F0.wireOp",EDGE,"E7"),sQuery(id+"F0.wireOp",EDGE,"E8"),sQuery(id+"F0.wireOp",EDGE,"E9"),sQuery(id+"F0.wireOp",EDGE,"E10"),sQuery(id+"F0.wireOp",EDGE,"E95"),sQuery(id+"F0.wireOp",EDGE,"E96"),sQuery(id+"F0.wireOp",EDGE,"E97"),sQuery(id+"F0.wireOp",EDGE,"E98"),sQuery(id+"F0.wireOp",EDGE,"E99"),sQuery(id+"F0.wireOp",EDGE,"E100")])],"isStart":true});
            var sketch = newSketch(context, id + "F5", { "sketchPlane" : qUnion([Q0])});
            skLineSegment(sketch, "E149", {"start": v(-8.55, 25) * mm, "end": v(0, 25) * mm});
            skLineSegment(sketch, "E150", {"start": v(0, 25) * mm, "end": v(8.55, 25) * mm});
            skLineSegment(sketch, "E151", {"start": v(25.93, -5.1) * mm, "end": v(21.65, -12.5) * mm});
            skLineSegment(sketch, "E152", {"start": v(21.65, -12.5) * mm, "end": v(17.38, -19.9) * mm});
            skLineSegment(sketch, "E153", {"start": v(-17.38, -19.9) * mm, "end": v(-21.65, -12.5) * mm});
            skLineSegment(sketch, "E154", {"start": v(-21.65, -12.5) * mm, "end": v(-25.93, -5.1) * mm});
            skLineSegment(sketch, "E155", {"start": v(0, 25) * mm, "end": v(0, 23) * mm});
            skLineSegment(sketch, "E156", {"start": v(21.65, -12.5) * mm, "end": v(19.92, -11.5) * mm});
            skLineSegment(sketch, "E157", {"start": v(-21.65, -12.5) * mm, "end": v(-19.92, -11.5) * mm});
            skLineSegment(sketch, "E158", {"start": v(0, 23) * mm, "end": v(1.5, 23) * mm});
            skLineSegment(sketch, "E159", {"start": v(0, 23) * mm, "end": v(-1.5, 23) * mm});
            skLineSegment(sketch, "E160", {"start": v(-19.92, -11.5) * mm, "end": v(-20.67, -10.2) * mm});
            skLineSegment(sketch, "E161", {"start": v(-19.92, -11.5) * mm, "end": v(-19.17, -12.8) * mm});
            skLineSegment(sketch, "E162", {"start": v(19.92, -11.5) * mm, "end": v(20.67, -10.2) * mm});
            skLineSegment(sketch, "E163", {"start": v(19.92, -11.5) * mm, "end": v(19.17, -12.8) * mm});
            skLineSegment(sketch, "E164", {"start": v(-20.67, -10.2) * mm, "end": v(-22.4, -11.2) * mm});
            skLineSegment(sketch, "E165", {"start": v(-19.17, -12.8) * mm, "end": v(-20.9, -13.8) * mm});
            skLineSegment(sketch, "E166", {"start": v(-1.5, 23) * mm, "end": v(-1.5, 25) * mm});
            skLineSegment(sketch, "E167", {"start": v(20.67, -10.2) * mm, "end": v(22.4, -11.2) * mm});
            skLineSegment(sketch, "E168", {"start": v(19.17, -12.8) * mm, "end": v(20.9, -13.8) * mm});
            skLineSegment(sketch, "E169", {"start": v(1.5, 23) * mm, "end": v(1.5, 25) * mm});
            skSolve(sketch);
        }
        {
            var Q0;
            {var subQ0=sQuery(id+"F5.wireOp",EDGE,"E155");Q0=makeQuery(id+"F5.imprint","IMPRINT",FACE,{"disambiguationData":[TD([[makeQuery(id+"F5.imprint","IMPRINT",EDGE,{"derivedFrom":subQ0}),-1.0]])]});}
            var Q1;
            {var subQ0=sQuery(id+"F5.wireOp",EDGE,"E155");Q1=makeQuery(id+"F5.imprint","IMPRINT",FACE,{"disambiguationData":[TD([[makeQuery(id+"F5.imprint","IMPRINT",EDGE,{"derivedFrom":subQ0}),1.0]])]});}
            var Q2;
            {var subQ0=sQuery(id+"F5.wireOp",EDGE,"E156");Q2=makeQuery(id+"F5.imprint","IMPRINT",FACE,{"disambiguationData":[TD([[makeQuery(id+"F5.imprint","IMPRINT",EDGE,{"derivedFrom":subQ0}),-1.0]])]});}
            var Q3;
            {var subQ0=sQuery(id+"F5.wireOp",EDGE,"E156");Q3=makeQuery(id+"F5.imprint","IMPRINT",FACE,{"disambiguationData":[TD([[makeQuery(id+"F5.imprint","IMPRINT",EDGE,{"derivedFrom":subQ0}),1.0]])]});}
            var Q4;
            {var subQ0=sQuery(id+"F5.wireOp",EDGE,"E157");Q4=makeQuery(id+"F5.imprint","IMPRINT",FACE,{"disambiguationData":[TD([[makeQuery(id+"F5.imprint","IMPRINT",EDGE,{"derivedFrom":subQ0}),1.0]])]});}
            var Q5;
            {var subQ0=sQuery(id+"F5.wireOp",EDGE,"E157");Q5=makeQuery(id+"F5.imprint","IMPRINT",FACE,{"disambiguationData":[TD([[makeQuery(id+"F5.imprint","IMPRINT",EDGE,{"derivedFrom":subQ0}),-1.0]])]});}
            extrude(context, id + "F6", {"entities" : qUnion([Q0, Q1, Q2, Q3, Q4, Q5]), "oppositeDirection" : true, "depth" : 2 * mm});
        }
        {
            var Q0;
            {var subQ3=sQuery(id+"F0.wireOp",EDGE,"E114");Q0=makeQuery(id+"F0.imprint","IMPRINT",FACE,{"disambiguationData":[TD([[makeQuery(id+"F0.imprint","IMPRINT",EDGE,{"derivedFrom":subQ3}),-1.0]])]});}
            var Q1;
            {var subQ0=sQuery(id+"F0.wireOp",EDGE,"E101");Q1=makeQuery(id+"F0.imprint","IMPRINT",FACE,{"disambiguationData":[TD([[makeQuery(id+"F0.imprint","IMPRINT",EDGE,{"derivedFrom":subQ0}),-1.0]])]});}
            var Q2;
            {var subQ0=sQuery(id+"F0.wireOp",EDGE,"E101");Q2=makeQuery(id+"F0.imprint","IMPRINT",FACE,{"disambiguationData":[TD([[makeQuery(id+"F0.imprint","IMPRINT",EDGE,{"derivedFrom":subQ0}),1.0]])]});}
            var Q3;
            {var subQ3=sQuery(id+"F0.wireOp",EDGE,"E103");Q3=makeQuery(id+"F0.imprint","IMPRINT",FACE,{"disambiguationData":[TD([[makeQuery(id+"F0.imprint","IMPRINT",EDGE,{"derivedFrom":subQ3}),1.0]])]});}
            var Q4;
            {var subQ3=sQuery(id+"F0.wireOp",EDGE,"E110");Q4=makeQuery(id+"F0.imprint","IMPRINT",FACE,{"disambiguationData":[TD([[makeQuery(id+"F0.imprint","IMPRINT",EDGE,{"derivedFrom":subQ3}),1.0]])]});}
            var Q5;
            {var subQ0=sQuery(id+"F0.wireOp",EDGE,"E108");Q5=makeQuery(id+"F0.imprint","IMPRINT",FACE,{"disambiguationData":[TD([[makeQuery(id+"F0.imprint","IMPRINT",EDGE,{"derivedFrom":subQ0}),-1.0]])]});}
            var Q6;
            {var subQ0=sQuery(id+"F0.wireOp",EDGE,"E108");Q6=makeQuery(id+"F0.imprint","IMPRINT",FACE,{"disambiguationData":[TD([[makeQuery(id+"F0.imprint","IMPRINT",EDGE,{"derivedFrom":subQ0}),1.0]])]});}
            var Q7;
            {var subQ3=sQuery(id+"F0.wireOp",EDGE,"E112");Q7=makeQuery(id+"F0.imprint","IMPRINT",FACE,{"disambiguationData":[TD([[makeQuery(id+"F0.imprint","IMPRINT",EDGE,{"derivedFrom":subQ3}),-1.0]])]});}
            var Q8;
            {var subQ0=sQuery(id+"F0.wireOp",EDGE,"E104");Q8=makeQuery(id+"F0.imprint","IMPRINT",FACE,{"disambiguationData":[TD([[makeQuery(id+"F0.imprint","IMPRINT",EDGE,{"derivedFrom":subQ0}),-1.0]])]});}
            var Q9;
            {var subQ0=sQuery(id+"F0.wireOp",EDGE,"E104");Q9=makeQuery(id+"F0.imprint","IMPRINT",FACE,{"disambiguationData":[TD([[makeQuery(id+"F0.imprint","IMPRINT",EDGE,{"derivedFrom":subQ0}),1.0]])]});}
            var Q10;
            {var subQ3=sQuery(id+"F0.wireOp",EDGE,"E107");Q10=makeQuery(id+"F0.imprint","IMPRINT",FACE,{"disambiguationData":[TD([[makeQuery(id+"F0.imprint","IMPRINT",EDGE,{"derivedFrom":subQ3}),1.0]])]});}
            var Q11;
            {var subQ3=sQuery(id+"F0.wireOp",EDGE,"E115");Q11=makeQuery(id+"F0.imprint","IMPRINT",FACE,{"disambiguationData":[TD([[makeQuery(id+"F0.imprint","IMPRINT",EDGE,{"derivedFrom":subQ3}),-1.0]])]});}
            extrude(context, id + "F7", {"entities" : qUnion([Q0, Q1, Q2, Q3, Q4, Q5, Q6, Q7, Q8, Q9, Q10, Q11]), "operationType" : NewBodyOperationType.ADD, "depth" : 6.3 * mm});
        }
        {
            var Q0;
            {var subQ3=sQuery(id+"F0.wireOp",EDGE,"E127");Q0=makeQuery(id+"F0.imprint","IMPRINT",FACE,{"disambiguationData":[TD([[makeQuery(id+"F0.imprint","IMPRINT",EDGE,{"derivedFrom":subQ3}),-1.0]])]});}
            var Q1;
            {var subQ3=sQuery(id+"F0.wireOp",EDGE,"E125");Q1=makeQuery(id+"F0.imprint","IMPRINT",FACE,{"disambiguationData":[TD([[makeQuery(id+"F0.imprint","IMPRINT",EDGE,{"derivedFrom":subQ3}),1.0]])]});}
            var Q2;
            {var subQ1=sQuery(id+"F0.wireOp",EDGE,"E23.0");var subQ3=sQuery(id+"F0.wireOp",EDGE,"E124");var subQ4=makeQuery(id+"F0.imprint","INTERSECT",VERTEX,{"derivedFrom":[subQ1,subQ3]});Q2=makeQuery(id+"F0.imprint","IMPRINT",FACE,{"disambiguationData":[TD([[makeQuery(id+"F0.imprint","IMPRINT",EDGE,{"disambiguationData":[TD([[subQ4,1.0]])],"derivedFrom":subQ3}),1.0]])]});}
            var Q3;
            {var subQ1=sQuery(id+"F0.wireOp",EDGE,"E23.2");var subQ3=sQuery(id+"F0.wireOp",EDGE,"E126");var subQ4=makeQuery(id+"F0.imprint","INTERSECT",VERTEX,{"derivedFrom":[subQ1,subQ3]});Q3=makeQuery(id+"F0.imprint","IMPRINT",FACE,{"disambiguationData":[TD([[makeQuery(id+"F0.imprint","IMPRINT",EDGE,{"disambiguationData":[TD([[subQ4,1.0]])],"derivedFrom":subQ3}),-1.0]])]});}
            var Q4;
            {var subQ1=sQuery(id+"F0.wireOp",EDGE,"E23.2");var subQ3=sQuery(id+"F0.wireOp",EDGE,"E122");var subQ4=makeQuery(id+"F0.imprint","INTERSECT",VERTEX,{"derivedFrom":[subQ1,subQ3]});Q4=makeQuery(id+"F0.imprint","IMPRINT",FACE,{"disambiguationData":[TD([[makeQuery(id+"F0.imprint","IMPRINT",EDGE,{"disambiguationData":[TD([[subQ4,1.0]])],"derivedFrom":subQ3}),1.0]])]});}
            var Q5;
            {var subQ1=sQuery(id+"F0.wireOp",EDGE,"E23.1");var subQ3=sQuery(id+"F0.wireOp",EDGE,"E120");var subQ4=makeQuery(id+"F0.imprint","INTERSECT",VERTEX,{"derivedFrom":[subQ1,subQ3]});Q5=makeQuery(id+"F0.imprint","IMPRINT",FACE,{"disambiguationData":[TD([[makeQuery(id+"F0.imprint","IMPRINT",EDGE,{"disambiguationData":[TD([[subQ4,1.0]])],"derivedFrom":subQ3}),-1.0]])]});}
            var Q6;
            {var subQ3=sQuery(id+"F0.wireOp",EDGE,"E121");Q6=makeQuery(id+"F0.imprint","IMPRINT",FACE,{"disambiguationData":[TD([[makeQuery(id+"F0.imprint","IMPRINT",EDGE,{"derivedFrom":subQ3}),-1.0]])]});}
            var Q7;
            {var subQ3=sQuery(id+"F0.wireOp",EDGE,"E123");Q7=makeQuery(id+"F0.imprint","IMPRINT",FACE,{"disambiguationData":[TD([[makeQuery(id+"F0.imprint","IMPRINT",EDGE,{"derivedFrom":subQ3}),1.0]])]});}
            var Q8;
            {var subQ3=sQuery(id+"F0.wireOp",EDGE,"E117");Q8=makeQuery(id+"F0.imprint","IMPRINT",FACE,{"disambiguationData":[TD([[makeQuery(id+"F0.imprint","IMPRINT",EDGE,{"derivedFrom":subQ3}),-1.0]])]});}
            var Q9;
            {var subQ1=sQuery(id+"F0.wireOp",EDGE,"E23.0");var subQ3=sQuery(id+"F0.wireOp",EDGE,"E116");var subQ4=makeQuery(id+"F0.imprint","INTERSECT",VERTEX,{"derivedFrom":[subQ1,subQ3]});Q9=makeQuery(id+"F0.imprint","IMPRINT",FACE,{"disambiguationData":[TD([[makeQuery(id+"F0.imprint","IMPRINT",EDGE,{"disambiguationData":[TD([[subQ4,1.0]])],"derivedFrom":subQ3}),-1.0]])]});}
            var Q10;
            {var subQ1=sQuery(id+"F0.wireOp",EDGE,"E23.1");var subQ3=sQuery(id+"F0.wireOp",EDGE,"E118");var subQ4=makeQuery(id+"F0.imprint","INTERSECT",VERTEX,{"derivedFrom":[subQ1,subQ3]});Q10=makeQuery(id+"F0.imprint","IMPRINT",FACE,{"disambiguationData":[TD([[makeQuery(id+"F0.imprint","IMPRINT",EDGE,{"disambiguationData":[TD([[subQ4,1.0]])],"derivedFrom":subQ3}),1.0]])]});}
            var Q11;
            {var subQ3=sQuery(id+"F0.wireOp",EDGE,"E119");Q11=makeQuery(id+"F0.imprint","IMPRINT",FACE,{"disambiguationData":[TD([[makeQuery(id+"F0.imprint","IMPRINT",EDGE,{"derivedFrom":subQ3}),1.0]])]});}
            extrude(context, id + "F8", {"entities" : qUnion([Q0, Q1, Q2, Q3, Q4, Q5, Q6, Q7, Q8, Q9, Q10, Q11]), "operationType" : NewBodyOperationType.ADD, "depth" : 6.3 * mm});
        }
        {
            var Q0;
            Q0=makeQuery(id+"F1.opExtrude","SWEPT_FACE",FACE,{"disambiguationData":[OSD([sQuery(id+"F0.wireOp",EDGE,"E5")])]});
            var sketch = newSketch(context, id + "F9", { "sketchPlane" : qUnion([Q0])});
            skLineSegment(sketch, "E170.bottom", {"start": v(-7.5, 100) * mm, "end": v(7.5, 100) * mm});
            skLineSegment(sketch, "E170.top", {"start": v(-7.5, 0) * mm, "end": v(7.5, 0) * mm});
            skLineSegment(sketch, "E170.left", {"start": v(-7.5, 100) * mm, "end": v(-7.5, 0) * mm});
            skLineSegment(sketch, "E170.right", {"start": v(7.5, 100) * mm, "end": v(7.5, 0) * mm});
            skLineSegment(sketch, "E171", {"start": v(-17.38, 100) * mm, "end": v(-7.5, 100) * mm});
            skLineSegment(sketch, "E172", {"start": v(7.5, 100) * mm, "end": v(17.38, 100) * mm});
            skLineSegment(sketch, "E173", {"start": v(0, 0) * mm, "end": v(0, 15) * mm});
            skLineSegment(sketch, "E174", {"start": v(0, 15) * mm, "end": v(-7.5, 28) * mm});
            skLineSegment(sketch, "E175", {"start": v(0, 15) * mm, "end": v(7.5, 28) * mm});
            skLineSegment(sketch, "E176", {"start": v(0, 100) * mm, "end": v(0, 85) * mm});
            skLineSegment(sketch, "E177", {"start": v(0, 85) * mm, "end": v(-7.5, 72) * mm});
            skLineSegment(sketch, "E178", {"start": v(0, 85) * mm, "end": v(7.5, 72) * mm});
            skSolve(sketch);
        }
        {
            var Q0;
            Q0=makeQuery(id+"F1.opExtrude","SWEPT_FACE",FACE,{"disambiguationData":[OSD([sQuery(id+"F0.wireOp",EDGE,"E6")])]});
            var sketch = newSketch(context, id + "F10", { "sketchPlane" : qUnion([Q0])});
            skLineSegment(sketch, "E179.bottom", {"start": v(-7.5, 100) * mm, "end": v(7.5, 100) * mm});
            skLineSegment(sketch, "E179.top", {"start": v(-7.5, 0) * mm, "end": v(7.5, 0) * mm});
            skLineSegment(sketch, "E179.left", {"start": v(-7.5, 100) * mm, "end": v(-7.5, 0) * mm});
            skLineSegment(sketch, "E179.right", {"start": v(7.5, 100) * mm, "end": v(7.5, 0) * mm});
            skLineSegment(sketch, "E180", {"start": v(-17.38, 100) * mm, "end": v(-7.5, 100) * mm});
            skLineSegment(sketch, "E181", {"start": v(7.5, 100) * mm, "end": v(17.38, 100) * mm});
            skLineSegment(sketch, "E182", {"start": v(0, 100) * mm, "end": v(0, 85) * mm});
            skLineSegment(sketch, "E183", {"start": v(0, 85) * mm, "end": v(-7.5, 72) * mm});
            skLineSegment(sketch, "E184", {"start": v(0, 85) * mm, "end": v(7.5, 72) * mm});
            skLineSegment(sketch, "E185", {"start": v(0, 0) * mm, "end": v(0, 15) * mm});
            skPoint(sketch, "E185.endSnap0", {"position": v(0, 0) * mm});
            skLineSegment(sketch, "E186", {"start": v(0, 15) * mm, "end": v(7.5, 28) * mm});
            skLineSegment(sketch, "E187", {"start": v(0, 15) * mm, "end": v(-7.5, 28) * mm});
            skSolve(sketch);
        }
        {
            var Q0;
            {var subQ0=sQuery(id+"F9.wireOp",EDGE,"E174");Q0=makeQuery(id+"F9.imprint","IMPRINT",FACE,{"disambiguationData":[TD([[makeQuery(id+"F9.imprint","IMPRINT",EDGE,{"derivedFrom":subQ0}),-1.0]])]});}
            extrude(context, id + "F11", {"entities" : qUnion([Q0]), "oppositeDirection" : true, "depth" : 10 * mm});
        }
        {
            var Q0;
            {var subQ3=sQuery(id+"F10.wireOp",EDGE,"E183");Q0=makeQuery(id+"F10.imprint","IMPRINT",FACE,{"disambiguationData":[TD([[makeQuery(id+"F10.imprint","IMPRINT",EDGE,{"derivedFrom":subQ3}),1.0]])]});}
            extrude(context, id + "F12", {"entities" : qUnion([Q0]), "oppositeDirection" : true, "depth" : 10 * mm});
        }
        {
            var Q0;
            Q0=makeQuery(id+"F4.opExtrude","SWEPT_BODY",BODY,{"disambiguationData":[OSD([sQuery(id+"F3.wireOp",EDGE,"E128"),sQuery(id+"F3.wireOp",EDGE,"E129"),sQuery(id+"F3.wireOp",EDGE,"E135"),sQuery(id+"F3.wireOp",EDGE,"E136"),sQuery(id+"F3.wireOp",EDGE,"E137"),sQuery(id+"F3.wireOp",EDGE,"E138")])]});
            var Q1;
            Q1=makeQuery(id+"F4.opExtrude","SWEPT_BODY",BODY,{"disambiguationData":[OSD([sQuery(id+"F3.wireOp",EDGE,"E130"),sQuery(id+"F3.wireOp",EDGE,"E131"),sQuery(id+"F3.wireOp",EDGE,"E140"),sQuery(id+"F3.wireOp",EDGE,"E141"),sQuery(id+"F3.wireOp",EDGE,"E142"),sQuery(id+"F3.wireOp",EDGE,"E143")])]});
            var Q2;
            Q2=makeQuery(id+"F4.opExtrude","SWEPT_BODY",BODY,{"disambiguationData":[OSD([sQuery(id+"F3.wireOp",EDGE,"E132"),sQuery(id+"F3.wireOp",EDGE,"E133"),sQuery(id+"F3.wireOp",EDGE,"E145"),sQuery(id+"F3.wireOp",EDGE,"E146"),sQuery(id+"F3.wireOp",EDGE,"E147"),sQuery(id+"F3.wireOp",EDGE,"E148")])]});
            var Q3;
            Q3=makeQuery(id+"F6.opExtrude","SWEPT_BODY",BODY,{"disambiguationData":[OSD([sQuery(id+"F5.wireOp",EDGE,"E149"),sQuery(id+"F5.wireOp",EDGE,"E150"),sQuery(id+"F5.wireOp",EDGE,"E158"),sQuery(id+"F5.wireOp",EDGE,"E159"),sQuery(id+"F5.wireOp",EDGE,"E166"),sQuery(id+"F5.wireOp",EDGE,"E169")])]});
            var Q4;
            Q4=makeQuery(id+"F6.opExtrude","SWEPT_BODY",BODY,{"disambiguationData":[OSD([sQuery(id+"F5.wireOp",EDGE,"E153"),sQuery(id+"F5.wireOp",EDGE,"E154"),sQuery(id+"F5.wireOp",EDGE,"E160"),sQuery(id+"F5.wireOp",EDGE,"E161"),sQuery(id+"F5.wireOp",EDGE,"E164"),sQuery(id+"F5.wireOp",EDGE,"E165")])]});
            var Q5;
            Q5=makeQuery(id+"F6.opExtrude","SWEPT_BODY",BODY,{"disambiguationData":[OSD([sQuery(id+"F5.wireOp",EDGE,"E151"),sQuery(id+"F5.wireOp",EDGE,"E152"),sQuery(id+"F5.wireOp",EDGE,"E162"),sQuery(id+"F5.wireOp",EDGE,"E163"),sQuery(id+"F5.wireOp",EDGE,"E167"),sQuery(id+"F5.wireOp",EDGE,"E168")])]});
            var Q6;
            Q6=makeQuery(id+"F11.opExtrude","SWEPT_BODY",BODY,{"disambiguationData":[OSD([sQuery(id+"F9.wireOp",EDGE,"E170.left"),sQuery(id+"F9.wireOp",EDGE,"E170.right"),sQuery(id+"F9.wireOp",EDGE,"E174"),sQuery(id+"F9.wireOp",EDGE,"E175"),sQuery(id+"F9.wireOp",EDGE,"E177"),sQuery(id+"F9.wireOp",EDGE,"E178")])]});
            var Q7;
            Q7=makeQuery(id+"F12.opExtrude","SWEPT_BODY",BODY,{"disambiguationData":[OSD([sQuery(id+"F10.wireOp",EDGE,"E179.left"),sQuery(id+"F10.wireOp",EDGE,"E179.right"),sQuery(id+"F10.wireOp",EDGE,"E183"),sQuery(id+"F10.wireOp",EDGE,"E184"),sQuery(id+"F10.wireOp",EDGE,"E186"),sQuery(id+"F10.wireOp",EDGE,"E187")])]});
            var Q8;
            Q8=makeQuery(id+"F1.opExtrude","SWEPT_BODY",BODY,{"disambiguationData":[OSD([sQuery(id+"F0.wireOp",EDGE,"E0.0"),sQuery(id+"F0.wireOp",EDGE,"E0.2"),sQuery(id+"F0.wireOp",EDGE,"E0.4"),sQuery(id+"F0.wireOp",EDGE,"E2"),sQuery(id+"F0.wireOp",EDGE,"E3"),sQuery(id+"F0.wireOp",EDGE,"E4"),sQuery(id+"F0.wireOp",EDGE,"E5"),sQuery(id+"F0.wireOp",EDGE,"E6"),sQuery(id+"F0.wireOp",EDGE,"E7"),sQuery(id+"F0.wireOp",EDGE,"E8"),sQuery(id+"F0.wireOp",EDGE,"E9"),sQuery(id+"F0.wireOp",EDGE,"E10")])]});
            booleanBodies(context, id + "F13", {"operationType" : BooleanOperationType.SUBTRACTION, "tools" : qUnion([Q0, Q1, Q2, Q3, Q4, Q5, Q6, Q7]), "targets" : qUnion([Q8])});
        }
        {
            var Q0;
            Q0=makeQuery(id+"F13.opBoolean","COPY",EDGE,{"derivedFrom":makeQuery(id+"F4.opExtrude","CAP_EDGE",EDGE,{"disambiguationData":[OSD([sQuery(id+"F3.wireOp",EDGE,"E128"),sQuery(id+"F3.wireOp",EDGE,"E129")])],"isStart":false})});
            var Q1;
            Q1=makeQuery(id+"F13.opBoolean","COPY",EDGE,{"derivedFrom":makeQuery(id+"F4.opExtrude","CAP_EDGE",EDGE,{"disambiguationData":[OSD([sQuery(id+"F3.wireOp",EDGE,"E130"),sQuery(id+"F3.wireOp",EDGE,"E131")])],"isStart":false})});
            var Q2;
            Q2=makeQuery(id+"F13.opBoolean","COPY",EDGE,{"derivedFrom":makeQuery(id+"F4.opExtrude","CAP_EDGE",EDGE,{"disambiguationData":[OSD([sQuery(id+"F3.wireOp",EDGE,"E132"),sQuery(id+"F3.wireOp",EDGE,"E133")])],"isStart":false})});
            var Q3;
            Q3=makeQuery(id+"F13.opBoolean","COPY",EDGE,{"derivedFrom":makeQuery(id+"F6.opExtrude","CAP_EDGE",EDGE,{"disambiguationData":[OSD([sQuery(id+"F5.wireOp",EDGE,"E149"),sQuery(id+"F5.wireOp",EDGE,"E150")])],"isStart":false})});
            var Q4;
            Q4=makeQuery(id+"F13.opBoolean","COPY",EDGE,{"derivedFrom":makeQuery(id+"F6.opExtrude","CAP_EDGE",EDGE,{"disambiguationData":[OSD([sQuery(id+"F5.wireOp",EDGE,"E153"),sQuery(id+"F5.wireOp",EDGE,"E154")])],"isStart":false})});
            var Q5;
            Q5=makeQuery(id+"F13.opBoolean","COPY",EDGE,{"derivedFrom":makeQuery(id+"F6.opExtrude","CAP_EDGE",EDGE,{"disambiguationData":[OSD([sQuery(id+"F5.wireOp",EDGE,"E151"),sQuery(id+"F5.wireOp",EDGE,"E152")])],"isStart":false})});
            var Q6;
            Q6=makeQuery(id+"F7.opExtrude","CAP_EDGE",EDGE,{"disambiguationData":[OSD([sQuery(id+"F0.wireOp",EDGE,"E102"),sQuery(id+"F0.wireOp",EDGE,"E113")])],"isStart":false});
            var Q7;
            Q7=makeQuery(id+"F7.opExtrude","CAP_EDGE",EDGE,{"disambiguationData":[OSD([sQuery(id+"F0.wireOp",EDGE,"E109"),sQuery(id+"F0.wireOp",EDGE,"E111")])],"isStart":false});
            var Q8;
            Q8=makeQuery(id+"F7.opExtrude","CAP_EDGE",EDGE,{"disambiguationData":[OSD([sQuery(id+"F0.wireOp",EDGE,"E105"),sQuery(id+"F0.wireOp",EDGE,"E106")])],"isStart":false});
            var Q9;
            Q9=makeQuery(id+"F8.opExtrude","CAP_EDGE",EDGE,{"disambiguationData":[OSD([sQuery(id+"F0.wireOp",EDGE,"E124"),sQuery(id+"F0.wireOp",EDGE,"E126")])],"isStart":false});
            var Q10;
            Q10=makeQuery(id+"F8.opExtrude","CAP_EDGE",EDGE,{"disambiguationData":[OSD([sQuery(id+"F0.wireOp",EDGE,"E116"),sQuery(id+"F0.wireOp",EDGE,"E118")])],"isStart":false});
            var Q11;
            Q11=makeQuery(id+"F8.opExtrude","CAP_EDGE",EDGE,{"disambiguationData":[OSD([sQuery(id+"F0.wireOp",EDGE,"E120"),sQuery(id+"F0.wireOp",EDGE,"E122")])],"isStart":false});
            chamfer(context, id + "F14", {"entities" : qUnion([Q0, Q1, Q2, Q3, Q4, Q5, Q6, Q7, Q8, Q9, Q10, Q11]), "width" : 2 * mm, "tangentPropagation" : true});
        }
    });
